# Revit family: rulonnie_protivopozarnie_vorota_firetechnics-r_ei60
name_source: partatom
category: Двери
revit_build: Autodesk Revit 2018 (Build: 20170223_1515(x64)
units: mm (PartAtom-declared; Revit-internal decimal feet)

## family parameters
Всегда вертикально = Да
Заголовок OmniClass = Doors
Номер OmniClass = 23.30.10.00
Общий = Нет
Основа = Стена
При загрузке вырезать с полостями = Нет
Точка расчета площади = Нет

## types (1)
- R EI60 c минеральным заполнителем
    ADSK_URL страницы изделия = https://www.fire-tec.ru
    ADSK_Завод-изготовитель = Firetechnics
    ADSK_Наименование = Рулонные противопожарные ворота FireTechnics-S EI60 с миниральным заполнителем
    ADSK_Предел огнестойкости = EI60
    ADSK_Размер_Высота = 3000 мм
    ADSK_Размер_Ширина = 3000 мм
    URL = https://www.fire-tec.ru
    Аналитическая конструкция = <Нет>
    Высота = 3000 мм
    Высота короба = 500 мм
    Длина направляющей = 60 мм
    Замыкание стены = По основе
    Изготовитель = Firetechnics
    Материал направляющих = Сталь_оцинкованная_листовая_2мм_Firetechnics
    Материал полотна = Полотно с наполнителем из минерального заполнителя Firetechnics
    Огнестойкость = EI60
    Отстаяние от двигателя = 330 мм
    Функция = Внутренние слои
    Ширина = 3000 мм
    Ширина верхней направляющей = 374 мм
    Ширина направляющих = 115 мм
    Ширина полотна = 75 мм
    ширина входа в полотна = 40 мм

## geometry (parser evidence)
native form markers: Blend x2
no freeform markers — native parametric forms only
